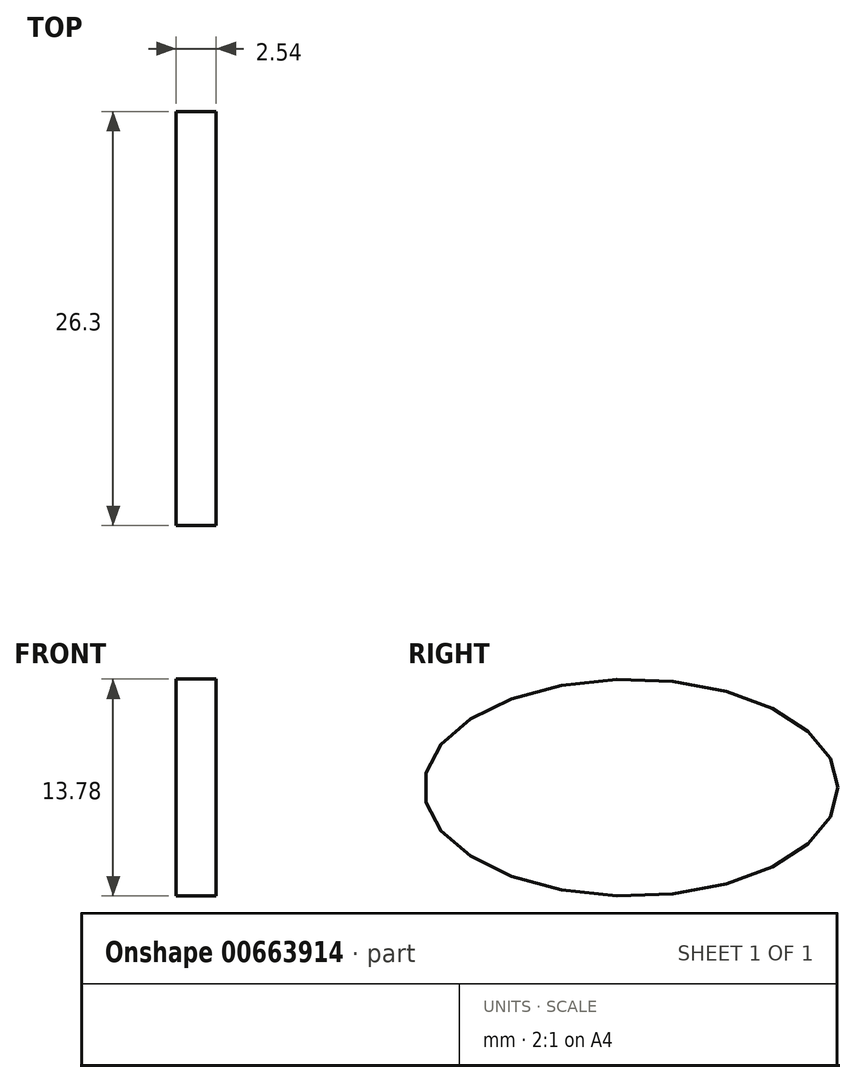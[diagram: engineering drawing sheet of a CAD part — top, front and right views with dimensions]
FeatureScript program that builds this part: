
annotation { "Feature Type Name" : "Feature", "Feature Type Description" : "" }
export const myFeature = defineFeature(function(context is Context, id is Id, definition is map)
    precondition{}
    {
        {
            var Q0;
            Q0=qCreatedBy(makeId("Right.planeOp"),FACE);
            var sketch = newSketch(context, id + "F0", { "sketchPlane" : qUnion([Q0])});
            skEllipse(sketch, "E0", {"center": v(-102.37, 51.27) * mm, "majorRadius": 13.15 * mm, "minorRadius": 6.89 * mm, "majorAxis": v(1, 0)});
            skSolve(sketch);
        }
        {
            var Q0;
            Q0 = qSketchRegion(id + "F0", true);
            extrude(context, id + "F1", {"entities" : qUnion([Q0]), "depth" : 2.54 * mm, "offsetDistance" : 25.4 * mm});
        }
    });
